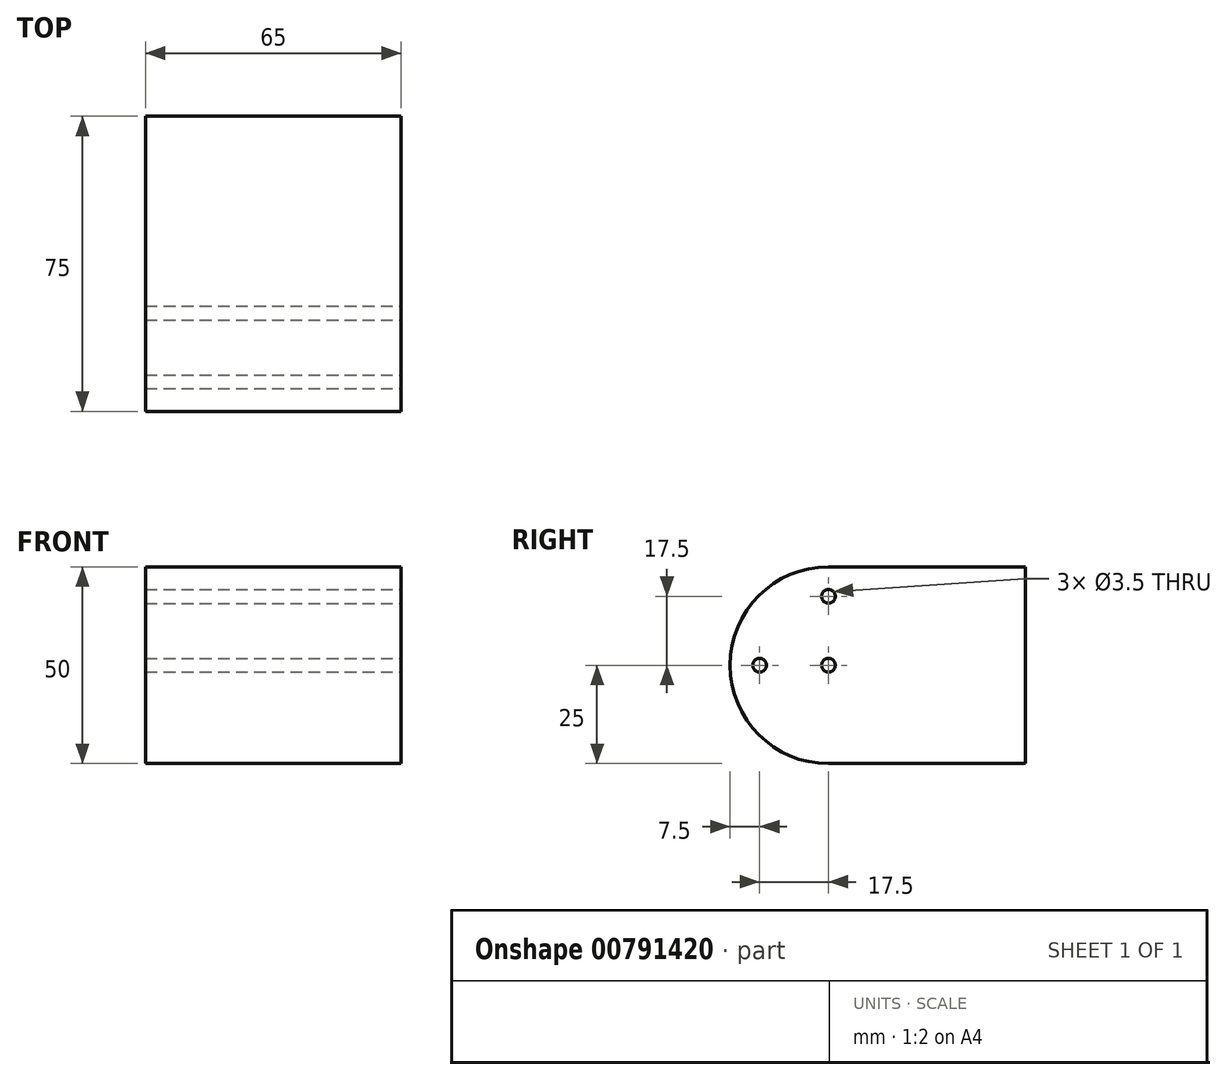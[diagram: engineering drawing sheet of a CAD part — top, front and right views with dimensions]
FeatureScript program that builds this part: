
annotation { "Feature Type Name" : "Feature", "Feature Type Description" : "" }
export const myFeature = defineFeature(function(context is Context, id is Id, definition is map)
    precondition{}
    {
        {
            var Q0;
            Q0=qCreatedBy(makeId("Right.planeOp"),FACE);
            var sketch = newSketch(context, id + "F0", { "sketchPlane" : qUnion([Q0])});
            skLineSegment(sketch, "E0.bottom", {"start": v(37.5, 25) * mm, "end": v(-12.5, 25) * mm});
            skLineSegment(sketch, "E0.top", {"start": v(37.5, -25) * mm, "end": v(-12.5, -25) * mm});
            skLineSegment(sketch, "E0.left", {"start": v(37.5, 25) * mm, "end": v(37.5, -25) * mm});
            skPoint(sketch, "E0.middle", {"position": v(0, 0) * mm});
            skArc(sketch, "E1", {"start": v(-12.5, 25) * mm, "mid": v(-37.5, 0) * mm, "end": v(-12.5, -25) * mm});
            skSolve(sketch);
        }
        {
            var Q0;
            Q0 = qSketchRegion(id + "F0", true);
            extrude(context, id + "F1", {"entities" : qUnion([Q0]), "depth" : 65 * mm, "offsetDistance" : 25 * mm});
        }
        {
            var Q0;
            Q0=makeQuery(id+"F1.opExtrude","CAP_FACE",FACE,{"disambiguationData":[OSD([sQuery(id+"F0.wireOp",EDGE,"E0.bottom"),sQuery(id+"F0.wireOp",EDGE,"E0.top"),sQuery(id+"F0.wireOp",EDGE,"E0.left"),sQuery(id+"F0.wireOp",EDGE,"E1")])],"isStart":false});
            var sketch = newSketch(context, id + "F2", { "sketchPlane" : qUnion([Q0])});
            skCircle(sketch, "E2", {"center": v(-12.5, 0) * mm, "radius": 1.75 * mm});
            skCircle(sketch, "E3", {"center": v(-12.5, 17.5) * mm, "radius": 1.75 * mm});
            skCircle(sketch, "E4", {"center": v(-30, 0) * mm, "radius": 1.75 * mm});
            skSolve(sketch);
        }
        {
            var Q0;
            Q0 = qSketchRegion(id + "F2", true);
            extrude(context, id + "F3", {"entities" : qUnion([Q0]), "operationType" : NewBodyOperationType.REMOVE, "oppositeDirection" : true, "depth" : 65 * mm, "offsetDistance" : 25 * mm});
        }
    });
